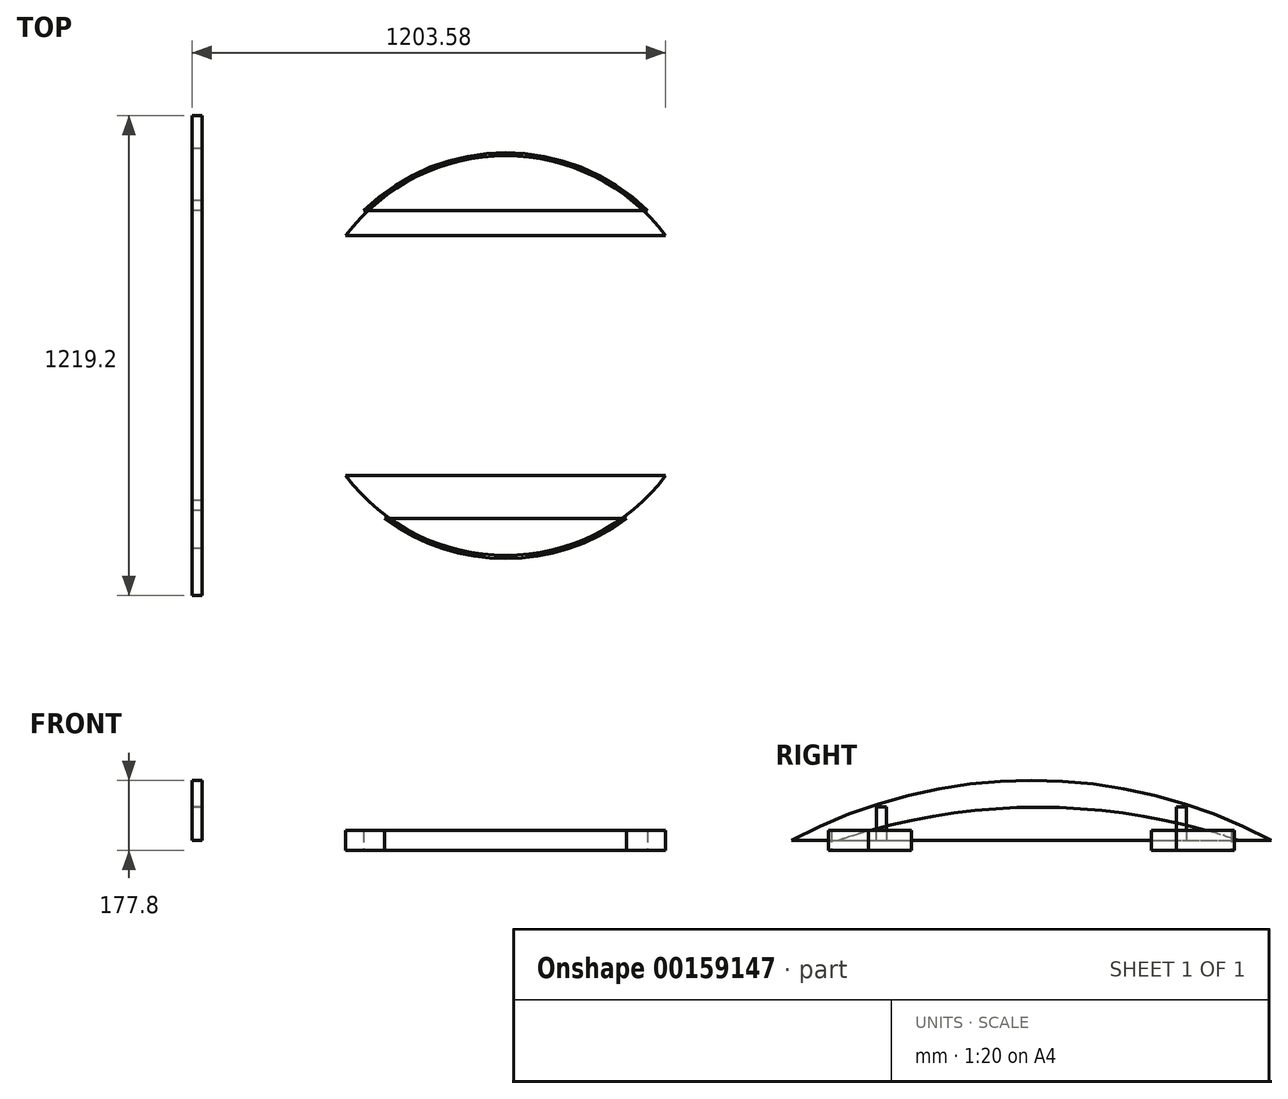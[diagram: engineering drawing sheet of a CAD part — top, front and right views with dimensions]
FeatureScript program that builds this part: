
annotation { "Feature Type Name" : "Feature", "Feature Type Description" : "" }
export const myFeature = defineFeature(function(context is Context, id is Id, definition is map)
    precondition{}
    {
        {
            var Q0;
            Q0=qCreatedBy(makeId("Right.planeOp"),FACE);
            var sketch = newSketch(context, id + "F0", { "sketchPlane" : qUnion([Q0])});
            skLineSegment(sketch, "E0", {"start": v(-609.27, 0) * mm, "end": v(-393.37, 0) * mm});
            skArc(sketch, "E1", {"start": v(609.93, 0) * mm, "mid": v(0.33, 152.4) * mm, "end": v(-609.27, 0) * mm});
            skLineSegment(sketch, "E2", {"start": v(-393.37, 0) * mm, "end": v(-393.37, 84.68) * mm});
            skLineSegment(sketch, "E3", {"start": v(-393.37, 84.68) * mm, "end": v(-367.97, 84.68) * mm});
            skLineSegment(sketch, "E4", {"start": v(-367.97, 84.68) * mm, "end": v(-367.97, 0) * mm});
            skLineSegment(sketch, "E5", {"start": v(-367.97, 0) * mm, "end": v(368.63, 0) * mm});
            skLineSegment(sketch, "E6", {"start": v(368.63, 0) * mm, "end": v(368.63, 84.68) * mm});
            skLineSegment(sketch, "E7", {"start": v(368.63, 84.68) * mm, "end": v(394.03, 84.68) * mm});
            skLineSegment(sketch, "E8", {"start": v(394.03, 84.68) * mm, "end": v(394.03, 0) * mm});
            skLineSegment(sketch, "E9", {"start": v(394.03, 0) * mm, "end": v(609.93, 0) * mm});
            skSolve(sketch);
        }
        {
            var Q0;
            Q0 = qSketchRegion(id + "F0", true);
            extrude(context, id + "F1", {"entities" : qUnion([Q0]), "depth" : 25.4 * mm, "symmetric" : true});
        }
        {
            var Q0;
            Q0=qCreatedBy(makeId("Right.planeOp"),FACE);
            var sketch = newSketch(context, id + "F2", { "sketchPlane" : qUnion([Q0])});
            skLineSegment(sketch, "E10", {"start": v(-490.64, 0) * mm, "end": v(525.36, 0) * mm});
            skArc(sketch, "E11", {"start": v(525.36, 0) * mm, "mid": v(17.36, 84.05) * mm, "end": v(-490.64, 0) * mm});
            skSolve(sketch);
        }
        {
            var Q0;
            Q0 = qSketchRegion(id + "F2", true);
            extrude(context, id + "F3", {"entities" : qUnion([Q0]), "depth" : 25.4 * mm, "symmetric" : true});
        }
        {
            var Q0;
            Q0=qCreatedBy(makeId("Top.planeOp"),FACE);
            var sketch = newSketch(context, id + "F4", { "sketchPlane" : qUnion([Q0])});
            skArc(sketch, "E12", {"start": v(1190.88, 304.8) * mm, "mid": v(784.48, 508) * mm, "end": v(378.08, 304.8) * mm});
            skLineSegment(sketch, "E13", {"start": v(378.08, 304.8) * mm, "end": v(1190.88, 304.8) * mm});
            skLineSegment(sketch, "E14", {"start": v(378.08, -304.8) * mm, "end": v(1190.88, -304.8) * mm});
            skArc(sketch, "E15.trimOffspring", {"start": v(378.08, -304.8) * mm, "mid": v(784.48, -508) * mm, "end": v(1190.88, -304.8) * mm});
            skSolve(sketch);
        }
        {
            var Q0;
            Q0 = qSketchRegion(id + "F4", true);
            extrude(context, id + "F5", {"entities" : qUnion([Q0]), "depth" : 50.8 * mm, "symmetric" : true});
        }
        {
            var Q0;
            Q0=qCreatedBy(makeId("Top.planeOp"),FACE);
            var sketch = newSketch(context, id + "F6", { "sketchPlane" : qUnion([Q0])});
            skArc(sketch, "E16", {"start": v(477.03, -414.36) * mm, "mid": v(784.36, -515.96) * mm, "end": v(1091.68, -414.36) * mm});
            skPoint(sketch, "E16.first.point", {"position": v(762.85, 514.8) * mm});
            skPoint(sketch, "E16.second.point", {"position": v(802.32, -515.64) * mm});
            skPoint(sketch, "E16.third.point", {"position": v(1217.17, -280.56) * mm});
            skLineSegment(sketch, "E17", {"start": v(423.71, 368.13) * mm, "end": v(1145, 368.13) * mm});
            skLineSegment(sketch, "E18", {"start": v(477.03, -414.36) * mm, "end": v(1091.68, -414.36) * mm});
            skArc(sketch, "E19.trimOffspring", {"start": v(1145, 368.13) * mm, "mid": v(784.36, 515.24) * mm, "end": v(423.71, 368.13) * mm});
            skSolve(sketch);
        }
        {
            var Q0;
            Q0 = qSketchRegion(id + "F6", true);
            extrude(context, id + "F7", {"entities" : qUnion([Q0]), "depth" : 50.8 * mm, "symmetric" : true});
        }
    });
